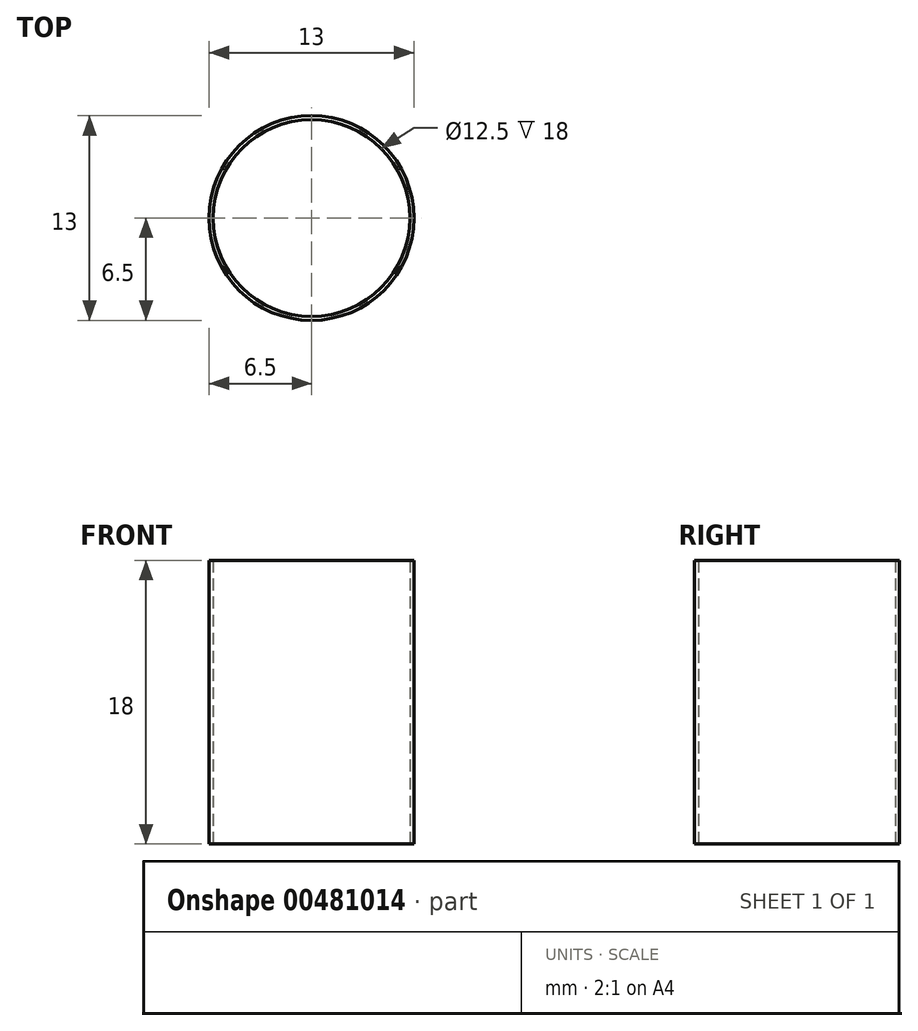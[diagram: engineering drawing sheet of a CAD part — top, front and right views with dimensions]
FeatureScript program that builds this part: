
annotation { "Feature Type Name" : "Feature", "Feature Type Description" : "" }
export const myFeature = defineFeature(function(context is Context, id is Id, definition is map)
    precondition{}
    {
        {
            var Q0;
            Q0=qCreatedBy(makeId("Top.planeOp"),FACE);
            var sketch = newSketch(context, id + "F0", { "sketchPlane" : qUnion([Q0])});
            skCircle(sketch, "E0", {"center": v(0, 0) * mm, "radius": 6.5 * mm});
            skCircle(sketch, "E1", {"center": v(0, 0) * mm, "radius": 6.25 * mm});
            skSolve(sketch);
        }
        {
            var Q0;
            Q0=makeQuery(id+"F0.imprint","IMPRINT",FACE,{"disambiguationData":[TD([[makeQuery(id+"F0.imprint","IMPRINT",EDGE,{"derivedFrom":sQuery(id+"F0.wireOp",EDGE,"E0")}),1.0]])]});
            extrude(context, id + "F1", {"entities" : qUnion([Q0]), "depth" : 18 * mm});
        }
    });
